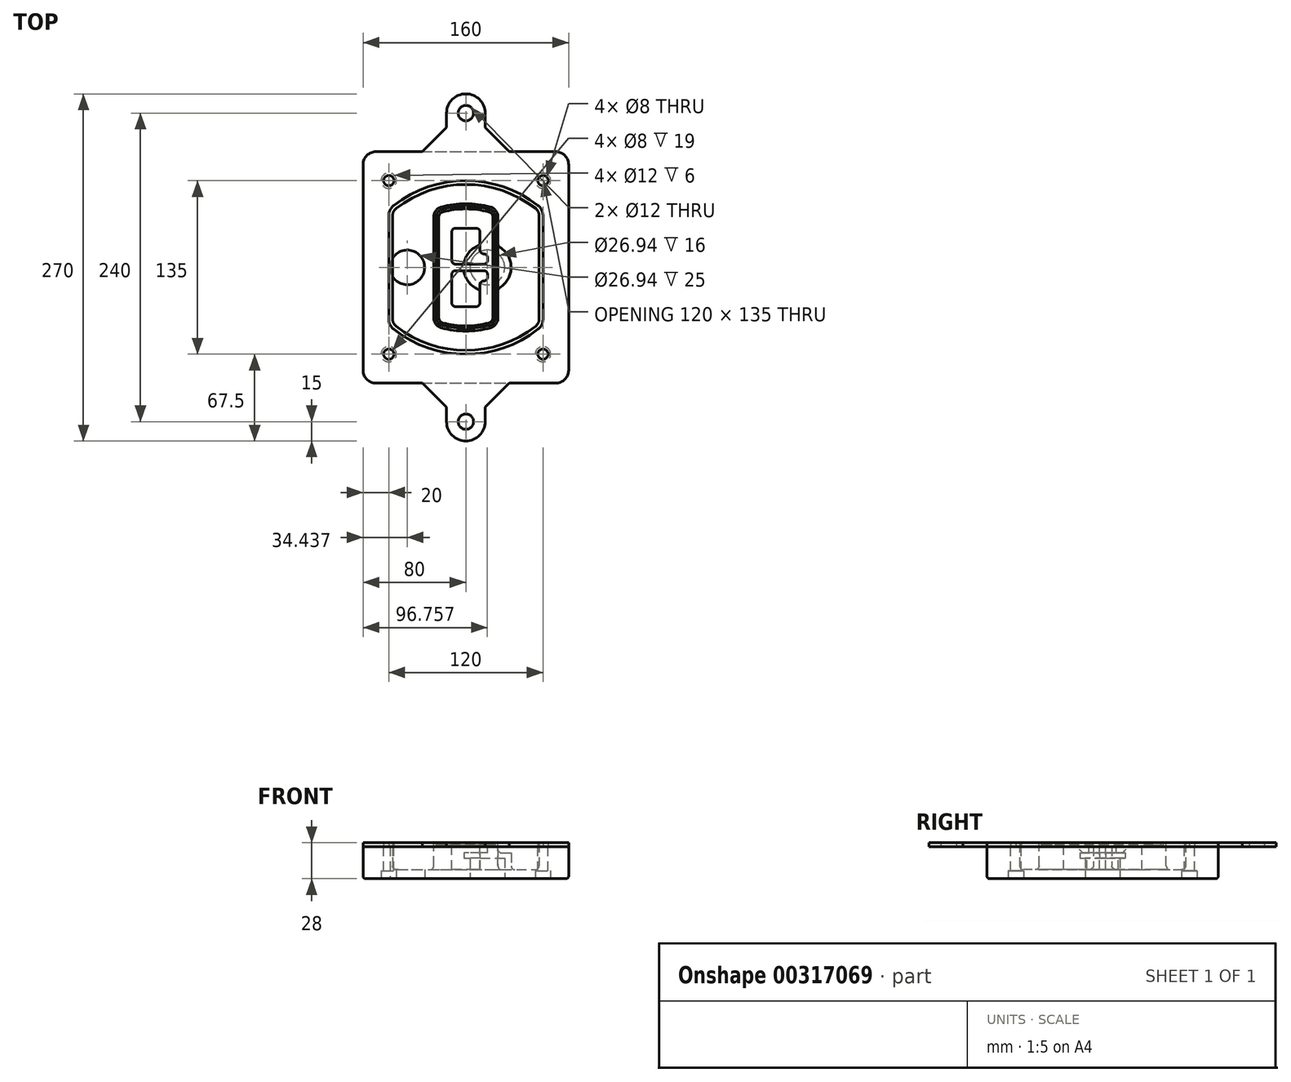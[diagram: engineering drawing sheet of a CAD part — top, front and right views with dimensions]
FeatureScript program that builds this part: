
annotation { "Feature Type Name" : "Feature", "Feature Type Description" : "" }
export const myFeature = defineFeature(function(context is Context, id is Id, definition is map)
    precondition{}
    {
        {
            var Q0;
            Q0=qCreatedBy(makeId("Top.planeOp"),FACE);
            var sketch = newSketch(context, id + "F0", { "sketchPlane" : qUnion([Q0])});
            skPoint(sketch, "E0.rect.middle", {"position": v(0, 0) * mm});
            skLineSegment(sketch, "E1.bottom", {"start": v(-70, -90) * mm, "end": v(70, -90) * mm});
            skLineSegment(sketch, "E1.top", {"start": v(-70, 90) * mm, "end": v(70, 90) * mm});
            skLineSegment(sketch, "E1.left", {"start": v(-80, -80) * mm, "end": v(-80, 80) * mm});
            skLineSegment(sketch, "E1.right", {"start": v(80, -80) * mm, "end": v(80, 80) * mm});
            skLineSegment(sketch, "E2", {"start": v(-80, 90) * mm, "end": v(80, -90) * mm, "construction": true});
            skLineSegment(sketch, "E3", {"start": v(80, 90) * mm, "end": v(-80, -90) * mm, "construction": true});
            skCircle(sketch, "E4", {"center": v(-60, 67.5) * mm, "radius": 4 * mm});
            skCircle(sketch, "E5", {"center": v(60, 67.5) * mm, "radius": 4 * mm});
            skCircle(sketch, "E6", {"center": v(60, -67.5) * mm, "radius": 4 * mm});
            skCircle(sketch, "E7", {"center": v(-60, -67.5) * mm, "radius": 4 * mm});
            skLineSegment(sketch, "E8", {"start": v(-60, 67.5) * mm, "end": v(60, 67.5) * mm, "construction": true});
            skLineSegment(sketch, "E9", {"start": v(60, 67.5) * mm, "end": v(60, -67.5) * mm, "construction": true});
            skLineSegment(sketch, "E10", {"start": v(60, -67.5) * mm, "end": v(-60, -67.5) * mm, "construction": true});
            skLineSegment(sketch, "E11", {"start": v(-60, -67.5) * mm, "end": v(-60, 67.5) * mm, "construction": true});
            skLineSegment(sketch, "E12", {"start": v(-60, 40.3) * mm, "end": v(-60, -40.3) * mm});
            skLineSegment(sketch, "E13", {"start": v(60, 40.3) * mm, "end": v(60, -40.3) * mm});
            skArc(sketch, "E14", {"start": v(56.15, 48.18) * mm, "mid": v(0, 67.5) * mm, "end": v(-56.15, 48.18) * mm});
            skArc(sketch, "E15", {"start": v(-56.15, -48.18) * mm, "mid": v(0, -67.5) * mm, "end": v(56.15, -48.18) * mm});
            skLineSegment(sketch, "E16", {"start": v(-60, 0) * mm, "end": v(60, 0) * mm, "construction": true});
            skPoint(sketch, "E17.visualSharp", {"position": v(-60, -45) * mm});
            skArc(sketch, "E17.filletArc", {"start": v(-60, -40.3) * mm, "mid": v(-58.99, -44.68) * mm, "end": v(-56.15, -48.18) * mm});
            skPoint(sketch, "E18.visualSharp", {"position": v(-60, 45) * mm});
            skArc(sketch, "E18.filletArc", {"start": v(-56.15, 48.18) * mm, "mid": v(-58.99, 44.68) * mm, "end": v(-60, 40.3) * mm});
            skPoint(sketch, "E19.visualSharp", {"position": v(60, 45) * mm});
            skArc(sketch, "E19.filletArc", {"start": v(60, 40.3) * mm, "mid": v(58.99, 44.68) * mm, "end": v(56.15, 48.18) * mm});
            skPoint(sketch, "E20.visualSharp", {"position": v(60, -45) * mm});
            skArc(sketch, "E20.filletArc", {"start": v(56.15, -48.18) * mm, "mid": v(58.99, -44.68) * mm, "end": v(60, -40.3) * mm});
            skPoint(sketch, "E21.visualSharp", {"position": v(-80, 90) * mm});
            skArc(sketch, "E21.filletArc", {"start": v(-70, 90) * mm, "mid": v(-77.07, 87.07) * mm, "end": v(-80, 80) * mm});
            skPoint(sketch, "E22.visualSharp", {"position": v(80, 90) * mm});
            skArc(sketch, "E22.filletArc", {"start": v(80, 80) * mm, "mid": v(77.07, 87.07) * mm, "end": v(70, 90) * mm});
            skPoint(sketch, "E23.visualSharp", {"position": v(80, -90) * mm});
            skArc(sketch, "E23.filletArc", {"start": v(70, -90) * mm, "mid": v(77.07, -87.07) * mm, "end": v(80, -80) * mm});
            skPoint(sketch, "E24.visualSharp", {"position": v(-80, -90) * mm});
            skArc(sketch, "E24.filletArc", {"start": v(-80, -80) * mm, "mid": v(-77.07, -87.07) * mm, "end": v(-70, -90) * mm});
            skArc(sketch, "E25.0", {"start": v(57, 40.3) * mm, "mid": v(56.3, 43.36) * mm, "end": v(54.3, 45.81) * mm});
            skLineSegment(sketch, "E25.1", {"start": v(57, 40.3) * mm, "end": v(57, -40.3) * mm});
            skArc(sketch, "E25.2", {"start": v(54.3, -45.81) * mm, "mid": v(56.3, -43.36) * mm, "end": v(57, -40.3) * mm});
            skArc(sketch, "E25.3", {"start": v(-54.3, -45.81) * mm, "mid": v(0, -64.5) * mm, "end": v(54.3, -45.81) * mm});
            skArc(sketch, "E25.4", {"start": v(-57, -40.3) * mm, "mid": v(-56.3, -43.36) * mm, "end": v(-54.3, -45.81) * mm});
            skArc(sketch, "E25.5", {"start": v(54.3, 45.81) * mm, "mid": v(0, 64.5) * mm, "end": v(-54.3, 45.81) * mm});
            skLineSegment(sketch, "E25.6", {"start": v(-57, 40.3) * mm, "end": v(-57, -40.3) * mm});
            skArc(sketch, "E25.7", {"start": v(-54.3, 45.81) * mm, "mid": v(-56.3, 43.36) * mm, "end": v(-57, 40.3) * mm});
            skArc(sketch, "E26.0", {"start": v(-58.62, 51.33) * mm, "mid": v(-62.58, 46.43) * mm, "end": v(-64, 40.3) * mm});
            skArc(sketch, "E26.1", {"start": v(58.62, 51.33) * mm, "mid": v(0, 71.5) * mm, "end": v(-58.62, 51.33) * mm});
            skArc(sketch, "E26.2", {"start": v(64, 40.3) * mm, "mid": v(62.58, 46.43) * mm, "end": v(58.62, 51.33) * mm});
            skLineSegment(sketch, "E26.3", {"start": v(64, 40.3) * mm, "end": v(64, -40.3) * mm});
            skArc(sketch, "E26.4", {"start": v(58.62, -51.33) * mm, "mid": v(62.58, -46.43) * mm, "end": v(64, -40.3) * mm});
            skLineSegment(sketch, "E26.5", {"start": v(-64, 40.3) * mm, "end": v(-64, -40.3) * mm});
            skArc(sketch, "E26.6", {"start": v(-58.62, -51.33) * mm, "mid": v(0, -71.5) * mm, "end": v(58.62, -51.33) * mm});
            skArc(sketch, "E26.7", {"start": v(-64, -40.3) * mm, "mid": v(-62.58, -46.43) * mm, "end": v(-58.62, -51.33) * mm});
            skSolve(sketch);
        }
        {
            var Q0;
            Q0=makeQuery(id+"F0.imprint","IMPRINT",FACE,{"disambiguationData":[TD([[makeQuery(id+"F0.imprint","IMPRINT",EDGE,{"derivedFrom":sQuery(id+"F0.wireOp",EDGE,"E1.bottom")}),1.0]])]});
            var Q1;
            Q1=makeQuery(id+"F0.imprint","IMPRINT",FACE,{"disambiguationData":[TD([[makeQuery(id+"F0.imprint","IMPRINT",EDGE,{"derivedFrom":sQuery(id+"F0.wireOp",EDGE,"E12")}),1.0]])]});
            var Q2;
            Q2=makeQuery(id+"F0.imprint","IMPRINT",FACE,{"disambiguationData":[TD([[makeQuery(id+"F0.imprint","IMPRINT",EDGE,{"derivedFrom":sQuery(id+"F0.wireOp",EDGE,"E25.0")}),1.0]])]});
            var Q3;
            Q3=makeQuery(id+"F0.imprint","IMPRINT",FACE,{"disambiguationData":[TD([[makeQuery(id+"F0.imprint","IMPRINT",EDGE,{"derivedFrom":sQuery(id+"F0.wireOp",EDGE,"E12")}),-1.0]])]});
            extrude(context, id + "F1", {"entities" : qUnion([Q0, Q1, Q2, Q3]), "oppositeDirection" : true, "depth" : 25 * mm});
        }
        {
            var Q0;
            Q0=makeQuery(id+"F0.imprint","IMPRINT",FACE,{"disambiguationData":[TD([[makeQuery(id+"F0.imprint","IMPRINT",EDGE,{"derivedFrom":sQuery(id+"F0.wireOp",EDGE,"E12")}),1.0]])]});
            extrude(context, id + "F2", {"entities" : qUnion([Q0]), "operationType" : NewBodyOperationType.ADD, "depth" : 3 * mm});
        }
        {
            var Q0;
            Q0=makeQuery(id+"F0.imprint","IMPRINT",FACE,{"disambiguationData":[TD([[makeQuery(id+"F0.imprint","IMPRINT",EDGE,{"derivedFrom":sQuery(id+"F0.wireOp",EDGE,"E25.0")}),1.0]])]});
            extrude(context, id + "F3", {"entities" : qUnion([Q0]), "operationType" : NewBodyOperationType.REMOVE, "oppositeDirection" : true, "depth" : 18 * mm});
        }
        {
            var Q0;
            Q0=makeQuery(id+"F2.opExtrude","CAP_FACE",FACE,{"disambiguationData":[OSD([sQuery(id+"F0.wireOp",EDGE,"E12"),sQuery(id+"F0.wireOp",EDGE,"E13"),sQuery(id+"F0.wireOp",EDGE,"E14"),sQuery(id+"F0.wireOp",EDGE,"E15"),sQuery(id+"F0.wireOp",EDGE,"E17.filletArc"),sQuery(id+"F0.wireOp",EDGE,"E18.filletArc"),sQuery(id+"F0.wireOp",EDGE,"E19.filletArc"),sQuery(id+"F0.wireOp",EDGE,"E20.filletArc"),sQuery(id+"F0.wireOp",EDGE,"E25.0"),sQuery(id+"F0.wireOp",EDGE,"E25.1"),sQuery(id+"F0.wireOp",EDGE,"E25.2"),sQuery(id+"F0.wireOp",EDGE,"E25.3"),sQuery(id+"F0.wireOp",EDGE,"E25.4"),sQuery(id+"F0.wireOp",EDGE,"E25.5"),sQuery(id+"F0.wireOp",EDGE,"E25.6"),sQuery(id+"F0.wireOp",EDGE,"E25.7")])],"isStart":false});
            var sketch = newSketch(context, id + "F4", { "sketchPlane" : qUnion([Q0])});
            skArc(sketch, "E27.0", {"start": v(-19.08, -46.97) * mm, "mid": v(0, -49.5) * mm, "end": v(19.08, -46.97) * mm});
            skArc(sketch, "E28.0", {"start": v(19.08, 46.97) * mm, "mid": v(0, 49.5) * mm, "end": v(-19.08, 46.97) * mm});
            skLineSegment(sketch, "E29", {"start": v(-25, 39.25) * mm, "end": v(-25, -39.25) * mm});
            skLineSegment(sketch, "E30", {"start": v(25, 39.25) * mm, "end": v(25, -39.25) * mm});
            skLineSegment(sketch, "E31", {"start": v(-25, 45.1) * mm, "end": v(25, 45.1) * mm, "construction": true});
            skLineSegment(sketch, "E32", {"start": v(-25, -45.1) * mm, "end": v(25, -45.1) * mm, "construction": true});
            skPoint(sketch, "E33.visualSharp", {"position": v(-25, 45.1) * mm});
            skArc(sketch, "E33.filletArc", {"start": v(-19.08, 46.97) * mm, "mid": v(-23.35, 44.11) * mm, "end": v(-25, 39.25) * mm});
            skPoint(sketch, "E34.visualSharp", {"position": v(25, 45.1) * mm});
            skArc(sketch, "E34.filletArc", {"start": v(25, 39.25) * mm, "mid": v(23.35, 44.11) * mm, "end": v(19.08, 46.97) * mm});
            skPoint(sketch, "E35.visualSharp", {"position": v(25, -45.1) * mm});
            skArc(sketch, "E35.filletArc", {"start": v(19.08, -46.97) * mm, "mid": v(23.35, -44.11) * mm, "end": v(25, -39.25) * mm});
            skPoint(sketch, "E36.visualSharp", {"position": v(-25, -45.1) * mm});
            skArc(sketch, "E36.filletArc", {"start": v(-25, -39.25) * mm, "mid": v(-23.35, -44.11) * mm, "end": v(-19.08, -46.97) * mm});
            skArc(sketch, "E37.0", {"start": v(54.3, 45.81) * mm, "mid": v(0, 64.5) * mm, "end": v(-54.3, 45.81) * mm});
            skArc(sketch, "E37.1", {"start": v(-54.3, 45.81) * mm, "mid": v(-56.3, 43.36) * mm, "end": v(-57, 40.3) * mm});
            skLineSegment(sketch, "E37.2", {"start": v(-57, 40.3) * mm, "end": v(-57, -40.3) * mm});
            skArc(sketch, "E37.3", {"start": v(-57, -40.3) * mm, "mid": v(-56.3, -43.36) * mm, "end": v(-54.3, -45.81) * mm});
            skArc(sketch, "E37.4", {"start": v(-54.3, -45.81) * mm, "mid": v(0, -64.5) * mm, "end": v(54.3, -45.81) * mm});
            skArc(sketch, "E37.5", {"start": v(54.3, -45.81) * mm, "mid": v(56.3, -43.36) * mm, "end": v(57, -40.3) * mm});
            skLineSegment(sketch, "E37.6", {"start": v(57, 40.3) * mm, "end": v(57, -40.3) * mm});
            skArc(sketch, "E37.7", {"start": v(57, 40.3) * mm, "mid": v(56.3, 43.36) * mm, "end": v(54.3, 45.81) * mm});
            skLineSegment(sketch, "E38.0", {"start": v(23, 39.25) * mm, "end": v(23, -39.25) * mm});
            skArc(sketch, "E38.1", {"start": v(18.56, -45.04) * mm, "mid": v(21.76, -42.9) * mm, "end": v(23, -39.25) * mm});
            skArc(sketch, "E38.2", {"start": v(-18.56, -45.04) * mm, "mid": v(0, -47.5) * mm, "end": v(18.56, -45.04) * mm});
            skArc(sketch, "E38.3", {"start": v(-23, -39.25) * mm, "mid": v(-21.76, -42.9) * mm, "end": v(-18.56, -45.04) * mm});
            skLineSegment(sketch, "E38.4", {"start": v(-23, 39.25) * mm, "end": v(-23, -39.25) * mm});
            skArc(sketch, "E38.5", {"start": v(23, 39.25) * mm, "mid": v(21.76, 42.9) * mm, "end": v(18.56, 45.04) * mm});
            skArc(sketch, "E38.6", {"start": v(-18.56, 45.04) * mm, "mid": v(-21.76, 42.9) * mm, "end": v(-23, 39.25) * mm});
            skArc(sketch, "E38.7", {"start": v(18.56, 45.04) * mm, "mid": v(0, 47.5) * mm, "end": v(-18.56, 45.04) * mm});
            skArc(sketch, "E39.0", {"start": v(21, 39.25) * mm, "mid": v(20.18, 41.68) * mm, "end": v(18.04, 43.1) * mm});
            skLineSegment(sketch, "E39.1", {"start": v(21, 39.25) * mm, "end": v(21, -39.25) * mm});
            skArc(sketch, "E39.2", {"start": v(18.04, -43.1) * mm, "mid": v(20.18, -41.68) * mm, "end": v(21, -39.25) * mm});
            skArc(sketch, "E39.3", {"start": v(-18.04, -43.1) * mm, "mid": v(0, -45.5) * mm, "end": v(18.04, -43.1) * mm});
            skArc(sketch, "E39.4", {"start": v(-21, -39.25) * mm, "mid": v(-20.18, -41.68) * mm, "end": v(-18.04, -43.1) * mm});
            skArc(sketch, "E39.5", {"start": v(18.04, 43.1) * mm, "mid": v(0, 45.5) * mm, "end": v(-18.04, 43.1) * mm});
            skLineSegment(sketch, "E39.6", {"start": v(-21, 39.25) * mm, "end": v(-21, -39.25) * mm});
            skArc(sketch, "E39.7", {"start": v(-18.04, 43.1) * mm, "mid": v(-20.18, 41.68) * mm, "end": v(-21, 39.25) * mm});
            skLineSegment(sketch, "E40", {"start": v(-25, 0) * mm, "end": v(25, 0) * mm, "construction": true});
            skLineSegment(sketch, "E41", {"start": v(-11, 5.5) * mm, "end": v(-11, 27.5) * mm});
            skLineSegment(sketch, "E42", {"start": v(-8, 30.5) * mm, "end": v(8, 30.5) * mm});
            skLineSegment(sketch, "E43", {"start": v(11, 27.5) * mm, "end": v(11, 13.5) * mm});
            skLineSegment(sketch, "E44", {"start": v(14, 10.5) * mm, "end": v(14, 10.5) * mm});
            skLineSegment(sketch, "E45", {"start": v(17, 7.5) * mm, "end": v(17, 5.5) * mm});
            skLineSegment(sketch, "E46", {"start": v(14, 2.5) * mm, "end": v(-8, 2.5) * mm});
            skPoint(sketch, "E47.visualSharp", {"position": v(-11, 30.5) * mm});
            skArc(sketch, "E47.filletArc", {"start": v(-8, 30.5) * mm, "mid": v(-10.12, 29.62) * mm, "end": v(-11, 27.5) * mm});
            skPoint(sketch, "E48.visualSharp", {"position": v(11, 30.5) * mm});
            skArc(sketch, "E48.filletArc", {"start": v(11, 27.5) * mm, "mid": v(10.12, 29.62) * mm, "end": v(8, 30.5) * mm});
            skPoint(sketch, "E49.visualSharp", {"position": v(11, 10.5) * mm});
            skArc(sketch, "E49.filletArc", {"start": v(11, 13.5) * mm, "mid": v(11.88, 11.38) * mm, "end": v(14, 10.5) * mm});
            skPoint(sketch, "E50.visualSharp", {"position": v(17, 10.5) * mm});
            skArc(sketch, "E50.filletArc", {"start": v(17, 7.5) * mm, "mid": v(16.12, 9.62) * mm, "end": v(14, 10.5) * mm});
            skPoint(sketch, "E51.visualSharp", {"position": v(17, 2.5) * mm});
            skArc(sketch, "E51.filletArc", {"start": v(14, 2.5) * mm, "mid": v(16.12, 3.38) * mm, "end": v(17, 5.5) * mm});
            skPoint(sketch, "E52.visualSharp", {"position": v(-11, 2.5) * mm});
            skArc(sketch, "E52.filletArc", {"start": v(-11, 5.5) * mm, "mid": v(-10.12, 3.38) * mm, "end": v(-8, 2.5) * mm});
            skLineSegment(sketch, "E53.0.MirrorCS", {"start": v(14, -2.5) * mm, "end": v(-8, -2.5) * mm});
            skArc(sketch, "E54.0.MirrorCS", {"start": v(-11, -5.5) * mm, "mid": v(-10.12, -3.38) * mm, "end": v(-8, -2.5) * mm});
            skLineSegment(sketch, "E55.0.MirrorCS", {"start": v(-11, -5.5) * mm, "end": v(-11, -27.5) * mm});
            skArc(sketch, "E56.0.MirrorCS", {"start": v(-8, -30.5) * mm, "mid": v(-10.12, -29.62) * mm, "end": v(-11, -27.5) * mm});
            skLineSegment(sketch, "E57.0.MirrorCS", {"start": v(-8, -30.5) * mm, "end": v(8, -30.5) * mm});
            skArc(sketch, "E58.0.MirrorCS", {"start": v(11, -27.5) * mm, "mid": v(10.12, -29.62) * mm, "end": v(8, -30.5) * mm});
            skLineSegment(sketch, "E59.0.MirrorCS", {"start": v(11, -27.5) * mm, "end": v(11, -13.5) * mm});
            skArc(sketch, "E60.0.MirrorCS", {"start": v(11, -13.5) * mm, "mid": v(11.88, -11.38) * mm, "end": v(14, -10.5) * mm});
            skArc(sketch, "E61.0.MirrorCS", {"start": v(17, -7.5) * mm, "mid": v(16.12, -9.62) * mm, "end": v(14, -10.5) * mm});
            skLineSegment(sketch, "E62.0.MirrorCS", {"start": v(17, -7.5) * mm, "end": v(17, -5.5) * mm});
            skArc(sketch, "E63.0.MirrorCS", {"start": v(14, -2.5) * mm, "mid": v(16.12, -3.38) * mm, "end": v(17, -5.5) * mm});
            skSolve(sketch);
        }
        {
            var Q0;
            Q0=makeQuery(id+"F4.imprint","IMPRINT",FACE,{"disambiguationData":[TD([[makeQuery(id+"F4.imprint","IMPRINT",EDGE,{"derivedFrom":sQuery(id+"F4.wireOp",EDGE,"E27.0")}),1.0]])]});
            var Q1;
            Q1=makeQuery(id+"F4.imprint","IMPRINT",FACE,{"disambiguationData":[TD([[makeQuery(id+"F4.imprint","IMPRINT",EDGE,{"derivedFrom":sQuery(id+"F4.wireOp",EDGE,"E38.0")}),-1.0]])]});
            var Q2;
            Q2=makeQuery(id+"F4.imprint","IMPRINT",FACE,{"disambiguationData":[TD([[makeQuery(id+"F4.imprint","IMPRINT",EDGE,{"derivedFrom":sQuery(id+"F4.wireOp",EDGE,"E39.0")}),1.0]])]});
            extrude(context, id + "F5", {"entities" : qUnion([Q0, Q1, Q2]), "operationType" : NewBodyOperationType.ADD, "endBound" : BoundingType.UP_TO_NEXT, "oppositeDirection" : true, "depth" : 25 * mm});
        }
        {
            var Q0;
            Q0=makeQuery(id+"F4.imprint","IMPRINT",FACE,{"disambiguationData":[TD([[makeQuery(id+"F4.imprint","IMPRINT",EDGE,{"derivedFrom":sQuery(id+"F4.wireOp",EDGE,"E38.0")}),-1.0]])]});
            extrude(context, id + "F6", {"entities" : qUnion([Q0]), "operationType" : NewBodyOperationType.REMOVE, "oppositeDirection" : true, "depth" : 2 * mm});
        }
        {
            var Q0;
            Q0=makeQuery(id+"F1.opExtrude","CAP_FACE",FACE,{"disambiguationData":[OSD([sQuery(id+"F0.wireOp",EDGE,"E1.bottom"),sQuery(id+"F0.wireOp",EDGE,"E1.top"),sQuery(id+"F0.wireOp",EDGE,"E1.left"),sQuery(id+"F0.wireOp",EDGE,"E1.right"),sQuery(id+"F0.wireOp",EDGE,"E4"),sQuery(id+"F0.wireOp",EDGE,"E5"),sQuery(id+"F0.wireOp",EDGE,"E6"),sQuery(id+"F0.wireOp",EDGE,"E7"),sQuery(id+"F0.wireOp",EDGE,"E21.filletArc"),sQuery(id+"F0.wireOp",EDGE,"E22.filletArc"),sQuery(id+"F0.wireOp",EDGE,"E23.filletArc"),sQuery(id+"F0.wireOp",EDGE,"E24.filletArc")])],"isStart":false});
            var sketch = newSketch(context, id + "F7", { "sketchPlane" : qUnion([Q0])});
            skCircle(sketch, "E64", {"center": v(16.76, 0) * mm, "radius": 13.47 * mm});
            skCircle(sketch, "E65", {"center": v(-45.56, 0) * mm, "radius": 13.47 * mm});
            skLineSegment(sketch, "E66", {"start": v(80, 0) * mm, "end": v(-80, 0) * mm});
            skCircle(sketch, "E67", {"center": v(16.76, 0) * mm, "radius": 18.47 * mm});
            skCircle(sketch, "E68", {"center": v(60, -67.5) * mm, "radius": 6 * mm});
            skCircle(sketch, "E69", {"center": v(-60, -67.5) * mm, "radius": 6 * mm});
            skCircle(sketch, "E70", {"center": v(-60, 67.5) * mm, "radius": 6 * mm});
            skCircle(sketch, "E71", {"center": v(60, 67.5) * mm, "radius": 6 * mm});
            skSolve(sketch);
        }
        {
            var Q0;
            {var subQ1=sQuery(id+"F7.wireOp",EDGE,"E66");var subQ4=sQuery(id+"F7.wireOp",EDGE,"E64");var subQ6=makeQuery(id+"F7.imprint","INTERSECT",VERTEX,{"disambiguationData":[OD(0.0)],"derivedFrom":[subQ4,subQ1]});Q0=makeQuery(id+"F7.imprint","IMPRINT",FACE,{"disambiguationData":[TD([[makeQuery(id+"F7.imprint","IMPRINT",EDGE,{"disambiguationData":[TD([[subQ6,-1.0]])],"derivedFrom":subQ4}),-1.0]])]});}
            var Q1;
            {var subQ0=sQuery(id+"F7.wireOp",EDGE,"E66");var subQ1=sQuery(id+"F7.wireOp",EDGE,"E64");var subQ3=makeQuery(id+"F7.imprint","INTERSECT",VERTEX,{"disambiguationData":[OD(0.0)],"derivedFrom":[subQ1,subQ0]});Q1=makeQuery(id+"F7.imprint","IMPRINT",FACE,{"disambiguationData":[TD([[makeQuery(id+"F7.imprint","IMPRINT",EDGE,{"disambiguationData":[TD([[subQ3,-1.0]])],"derivedFrom":subQ1}),1.0]])]});}
            var Q2;
            {var subQ0=sQuery(id+"F7.wireOp",EDGE,"E66");var subQ1=sQuery(id+"F7.wireOp",EDGE,"E64");var subQ3=makeQuery(id+"F7.imprint","INTERSECT",VERTEX,{"disambiguationData":[OD(0.0)],"derivedFrom":[subQ1,subQ0]});Q2=makeQuery(id+"F7.imprint","IMPRINT",FACE,{"disambiguationData":[TD([[makeQuery(id+"F7.imprint","IMPRINT",EDGE,{"disambiguationData":[TD([[subQ3,1.0]])],"derivedFrom":subQ1}),1.0]])]});}
            var Q3;
            {var subQ1=sQuery(id+"F7.wireOp",EDGE,"E66");var subQ4=sQuery(id+"F7.wireOp",EDGE,"E64");var subQ6=makeQuery(id+"F7.imprint","INTERSECT",VERTEX,{"disambiguationData":[OD(0.0)],"derivedFrom":[subQ4,subQ1]});Q3=makeQuery(id+"F7.imprint","IMPRINT",FACE,{"disambiguationData":[TD([[makeQuery(id+"F7.imprint","IMPRINT",EDGE,{"disambiguationData":[TD([[subQ6,1.0]])],"derivedFrom":subQ4}),-1.0]])]});}
            extrude(context, id + "F8", {"entities" : qUnion([Q0, Q1, Q2, Q3]), "operationType" : NewBodyOperationType.ADD, "oppositeDirection" : true, "depth" : 20 * mm});
        }
        {
            var Q0;
            {var subQ0=sQuery(id+"F7.wireOp",EDGE,"E66");var subQ1=sQuery(id+"F7.wireOp",EDGE,"E64");var subQ3=makeQuery(id+"F7.imprint","INTERSECT",VERTEX,{"disambiguationData":[OD(0.0)],"derivedFrom":[subQ1,subQ0]});Q0=makeQuery(id+"F7.imprint","IMPRINT",FACE,{"disambiguationData":[TD([[makeQuery(id+"F7.imprint","IMPRINT",EDGE,{"disambiguationData":[TD([[subQ3,-1.0]])],"derivedFrom":subQ1}),1.0]])]});}
            var Q1;
            {var subQ0=sQuery(id+"F7.wireOp",EDGE,"E66");var subQ1=sQuery(id+"F7.wireOp",EDGE,"E64");var subQ3=makeQuery(id+"F7.imprint","INTERSECT",VERTEX,{"disambiguationData":[OD(0.0)],"derivedFrom":[subQ1,subQ0]});Q1=makeQuery(id+"F7.imprint","IMPRINT",FACE,{"disambiguationData":[TD([[makeQuery(id+"F7.imprint","IMPRINT",EDGE,{"disambiguationData":[TD([[subQ3,1.0]])],"derivedFrom":subQ1}),1.0]])]});}
            extrude(context, id + "F9", {"entities" : qUnion([Q0, Q1]), "operationType" : NewBodyOperationType.REMOVE, "oppositeDirection" : true, "depth" : 16 * mm});
        }
        {
            var Q0;
            {var subQ0=sQuery(id+"F7.wireOp",EDGE,"E66");var subQ1=sQuery(id+"F7.wireOp",EDGE,"E65");var subQ3=makeQuery(id+"F7.imprint","INTERSECT",VERTEX,{"disambiguationData":[OD(0.0)],"derivedFrom":[subQ1,subQ0]});Q0=makeQuery(id+"F7.imprint","IMPRINT",FACE,{"disambiguationData":[TD([[makeQuery(id+"F7.imprint","IMPRINT",EDGE,{"disambiguationData":[TD([[subQ3,-1.0]])],"derivedFrom":subQ1}),1.0]])]});}
            var Q1;
            {var subQ0=sQuery(id+"F7.wireOp",EDGE,"E66");var subQ1=sQuery(id+"F7.wireOp",EDGE,"E65");var subQ3=makeQuery(id+"F7.imprint","INTERSECT",VERTEX,{"disambiguationData":[OD(0.0)],"derivedFrom":[subQ1,subQ0]});Q1=makeQuery(id+"F7.imprint","IMPRINT",FACE,{"disambiguationData":[TD([[makeQuery(id+"F7.imprint","IMPRINT",EDGE,{"disambiguationData":[TD([[subQ3,1.0]])],"derivedFrom":subQ1}),1.0]])]});}
            extrude(context, id + "F10", {"entities" : qUnion([Q0, Q1]), "operationType" : NewBodyOperationType.REMOVE, "oppositeDirection" : true, "depth" : 25 * mm});
        }
        {
            var Q0;
            Q0=makeQuery(id+"F7.imprint","IMPRINT",FACE,{"disambiguationData":[TD([[makeQuery(id+"F7.imprint","IMPRINT",EDGE,{"derivedFrom":sQuery(id+"F7.wireOp",EDGE,"E68")}),1.0]])]});
            var Q1;
            Q1=makeQuery(id+"F7.imprint","IMPRINT",FACE,{"disambiguationData":[TD([[makeQuery(id+"F7.imprint","IMPRINT",EDGE,{"derivedFrom":makeQuery(id+"F1.opExtrude","CAP_EDGE",EDGE,{"disambiguationData":[OSD([sQuery(id+"F0.wireOp",EDGE,"E5")])],"isStart":false})}),-1.0]])]});
            var Q2;
            Q2=makeQuery(id+"F7.imprint","IMPRINT",FACE,{"disambiguationData":[TD([[makeQuery(id+"F7.imprint","IMPRINT",EDGE,{"derivedFrom":sQuery(id+"F7.wireOp",EDGE,"E69")}),1.0]])]});
            var Q3;
            Q3=makeQuery(id+"F7.imprint","IMPRINT",FACE,{"disambiguationData":[TD([[makeQuery(id+"F7.imprint","IMPRINT",EDGE,{"derivedFrom":makeQuery(id+"F1.opExtrude","CAP_EDGE",EDGE,{"disambiguationData":[OSD([sQuery(id+"F0.wireOp",EDGE,"E4")])],"isStart":false})}),-1.0]])]});
            var Q4;
            Q4=makeQuery(id+"F7.imprint","IMPRINT",FACE,{"disambiguationData":[TD([[makeQuery(id+"F7.imprint","IMPRINT",EDGE,{"derivedFrom":sQuery(id+"F7.wireOp",EDGE,"E70")}),1.0]])]});
            var Q5;
            Q5=makeQuery(id+"F7.imprint","IMPRINT",FACE,{"disambiguationData":[TD([[makeQuery(id+"F7.imprint","IMPRINT",EDGE,{"derivedFrom":makeQuery(id+"F1.opExtrude","CAP_EDGE",EDGE,{"disambiguationData":[OSD([sQuery(id+"F0.wireOp",EDGE,"E7")])],"isStart":false})}),-1.0]])]});
            var Q6;
            Q6=makeQuery(id+"F7.imprint","IMPRINT",FACE,{"disambiguationData":[TD([[makeQuery(id+"F7.imprint","IMPRINT",EDGE,{"derivedFrom":sQuery(id+"F7.wireOp",EDGE,"E71")}),1.0]])]});
            var Q7;
            Q7=makeQuery(id+"F7.imprint","IMPRINT",FACE,{"disambiguationData":[TD([[makeQuery(id+"F7.imprint","IMPRINT",EDGE,{"derivedFrom":makeQuery(id+"F1.opExtrude","CAP_EDGE",EDGE,{"disambiguationData":[OSD([sQuery(id+"F0.wireOp",EDGE,"E6")])],"isStart":false})}),-1.0]])]});
            extrude(context, id + "F11", {"entities" : qUnion([Q0, Q1, Q2, Q3, Q4, Q5, Q6, Q7]), "operationType" : NewBodyOperationType.REMOVE, "oppositeDirection" : true, "depth" : 6 * mm});
        }
        {
            var Q0;
            Q0=makeQuery(id+"F9.boolean.opBoolean","COPY",FACE,{"derivedFrom":makeQuery(id+"F9.opExtrude","CAP_FACE",FACE,{"disambiguationData":[OSD([sQuery(id+"F7.wireOp",EDGE,"E64")])],"isStart":false})});
            var sketch = newSketch(context, id + "F12", { "sketchPlane" : qUnion([Q0])});
            skArc(sketch, "E72.0", {"start": v(11, 17.55) * mm, "mid": v(2.57, 11.82) * mm, "end": v(-1.54, 2.5) * mm});
            skArc(sketch, "E72.1", {"start": v(-1.54, -2.5) * mm, "mid": v(2.57, -11.82) * mm, "end": v(11, -17.55) * mm});
            skLineSegment(sketch, "E73", {"start": v(-1.54, -2.5) * mm, "end": v(14, -2.5) * mm});
            skLineSegment(sketch, "E74.0", {"start": v(14, 2.5) * mm, "end": v(-1.54, 2.5) * mm});
            skArc(sketch, "E74.1", {"start": v(14, 2.5) * mm, "mid": v(16.12, 3.38) * mm, "end": v(17, 5.5) * mm});
            skLineSegment(sketch, "E74.2", {"start": v(17, 7.5) * mm, "end": v(17, 5.5) * mm});
            skArc(sketch, "E74.3", {"start": v(17, 7.5) * mm, "mid": v(16.12, 9.62) * mm, "end": v(14, 10.5) * mm});
            skArc(sketch, "E74.4", {"start": v(11, 13.5) * mm, "mid": v(11.88, 11.38) * mm, "end": v(14, 10.5) * mm});
            skLineSegment(sketch, "E74.5", {"start": v(11, 17.55) * mm, "end": v(11, 13.5) * mm});
            skLineSegment(sketch, "E74.7", {"start": v(14, -2.5) * mm, "end": v(-1.54, -2.5) * mm});
            skArc(sketch, "E74.8", {"start": v(14, -2.5) * mm, "mid": v(16.12, -3.38) * mm, "end": v(17, -5.5) * mm});
            skLineSegment(sketch, "E74.9", {"start": v(17, -7.5) * mm, "end": v(17, -5.5) * mm});
            skArc(sketch, "E74.10", {"start": v(17, -7.5) * mm, "mid": v(16.12, -9.62) * mm, "end": v(14, -10.5) * mm});
            skArc(sketch, "E74.11", {"start": v(11, -13.5) * mm, "mid": v(11.88, -11.38) * mm, "end": v(14, -10.5) * mm});
            skLineSegment(sketch, "E74.12", {"start": v(11, -17.55) * mm, "end": v(11, -13.5) * mm});
            skPoint(sketch, "E75.orphan", {"position": v(11, -27.5) * mm});
            skPoint(sketch, "E76.orphan", {"position": v(-8, -2.5) * mm});
            skPoint(sketch, "E77.orphan", {"position": v(-8, 2.5) * mm});
            skPoint(sketch, "E78.orphan", {"position": v(11, 27.5) * mm});
            skSolve(sketch);
        }
        {
            var Q0;
            {var subQ7=sQuery(id+"F12.wireOp",EDGE,"E72.0");var subQ14=sQuery(id+"F12.wireOp",EDGE,"E72.1");var subQ16=sQuery(id+"F12.wireOp",EDGE,"E74.1");var subQ18=sQuery(id+"F12.wireOp",EDGE,"E74.8");Q0=qUnion([makeQuery(id+"F12.imprint","IMPRINT",FACE,{"disambiguationData":[TD([[makeQuery(id+"F12.imprint","IMPRINT",EDGE,{"derivedFrom":subQ7}),1.0]])]}),makeQuery(id+"F12.imprint","IMPRINT",FACE,{"disambiguationData":[TD([[makeQuery(id+"F12.imprint","IMPRINT",EDGE,{"derivedFrom":subQ14}),1.0]])]}),makeQuery(id+"F12.imprint","IMPRINT",FACE,{"disambiguationData":[TD([[makeQuery(id+"F12.imprint","IMPRINT",EDGE,{"derivedFrom":subQ16}),1.0]])]}),makeQuery(id+"F12.imprint","IMPRINT",FACE,{"disambiguationData":[TD([[makeQuery(id+"F12.imprint","IMPRINT",EDGE,{"derivedFrom":subQ18}),-1.0]])]})]);}
            var Q1;
            Q1=makeQuery(id+"F5.boolean.opBoolean","SPLIT",FACE,{"disambiguationData":[TD([makeQuery(id+"F5.opExtrude","SWEPT_FACE",FACE,{"disambiguationData":[OSD([sQuery(id+"F4.wireOp",EDGE,"E41")])]})])],"derivedFrom":makeQuery(id+"F3.boolean.opBoolean","COPY",FACE,{"derivedFrom":makeQuery(id+"F3.opExtrude","CAP_FACE",FACE,{"disambiguationData":[OSD([sQuery(id+"F0.wireOp",EDGE,"E25.0"),sQuery(id+"F0.wireOp",EDGE,"E25.1"),sQuery(id+"F0.wireOp",EDGE,"E25.2"),sQuery(id+"F0.wireOp",EDGE,"E25.3"),sQuery(id+"F0.wireOp",EDGE,"E25.4"),sQuery(id+"F0.wireOp",EDGE,"E25.5"),sQuery(id+"F0.wireOp",EDGE,"E25.6"),sQuery(id+"F0.wireOp",EDGE,"E25.7")])],"isStart":false})})});
            extrude(context, id + "F13", {"entities" : qUnion([Q0]), "operationType" : NewBodyOperationType.REMOVE, "endBound" : BoundingType.UP_TO_SURFACE, "endBoundEntityFace" : qUnion([Q1]), "depth" : 25 * mm});
        }
        {
            var Q0;
            Q0=makeQuery(id+"F3.boolean.opBoolean","COPY",EDGE,{"derivedFrom":makeQuery(id+"F3.opExtrude","CAP_EDGE",EDGE,{"disambiguationData":[OSD([sQuery(id+"F0.wireOp",EDGE,"E25.6")])],"isStart":false})});
            var Q1;
            Q1=makeQuery(id+"F8.boolean.opBoolean","INTERSECT",EDGE,{"derivedFrom":[makeQuery(id+"F5.opExtrude","SWEPT_FACE",FACE,{"disambiguationData":[OSD([sQuery(id+"F4.wireOp",EDGE,"E30")])]}),makeQuery(id+"F8.opExtrude","CAP_FACE",FACE,{"disambiguationData":[OSD([sQuery(id+"F7.wireOp",EDGE,"E67")])],"isStart":false})]});
            var Q2;
            Q2=makeQuery(id+"F8.boolean.opBoolean","INTERSECT",EDGE,{"disambiguationData":[OD(1.0)],"derivedFrom":[makeQuery(id+"F5.opExtrude","SWEPT_FACE",FACE,{"disambiguationData":[OSD([sQuery(id+"F4.wireOp",EDGE,"E30")])]}),makeQuery(id+"F8.opExtrude","SWEPT_FACE",FACE,{"disambiguationData":[OSD([sQuery(id+"F7.wireOp",EDGE,"E67")])]})]});
            var Q3;
            {var subQ0=sQuery(id+"F4.wireOp",EDGE,"E30");Q3=makeQuery(id+"F8.boolean.opBoolean","SPLIT",EDGE,{"disambiguationData":[TD([makeQuery(id+"F5.opExtrude","SWEPT_FACE",FACE,{"disambiguationData":[OSD([sQuery(id+"F4.wireOp",EDGE,"E35.filletArc")])]})])],"derivedFrom":makeQuery(id+"F5.opExtrude","CAP_EDGE",EDGE,{"disambiguationData":[OSD([subQ0])],"isStart":false})});}
            var Q4;
            {var subQ0=sQuery(id+"F0.wireOp",EDGE,"E25.7");var subQ1=sQuery(id+"F0.wireOp",EDGE,"E25.1");var subQ2=sQuery(id+"F0.wireOp",EDGE,"E25.6");var subQ3=sQuery(id+"F0.wireOp",EDGE,"E25.5");var subQ4=sQuery(id+"F0.wireOp",EDGE,"E25.4");var subQ5=sQuery(id+"F0.wireOp",EDGE,"E25.0");var subQ6=sQuery(id+"F0.wireOp",EDGE,"E25.2");var subQ7=sQuery(id+"F0.wireOp",EDGE,"E25.3");Q4=makeQuery(id+"F8.boolean.opBoolean","INTERSECT",EDGE,{"derivedFrom":[makeQuery(id+"F5.boolean.opBoolean","SPLIT",FACE,{"disambiguationData":[TD([makeQuery(id+"F2.opExtrude","SWEPT_FACE",FACE,{"disambiguationData":[OSD([subQ5])]})])],"derivedFrom":makeQuery(id+"F3.boolean.opBoolean","COPY",FACE,{"derivedFrom":makeQuery(id+"F3.opExtrude","CAP_FACE",FACE,{"disambiguationData":[OSD([subQ5,subQ1,subQ6,subQ7,subQ4,subQ3,subQ2,subQ0])],"isStart":false})})}),makeQuery(id+"F8.opExtrude","SWEPT_FACE",FACE,{"disambiguationData":[OSD([sQuery(id+"F7.wireOp",EDGE,"E67")])]})]});}
            var Q5;
            Q5=makeQuery(id+"F8.boolean.opBoolean","INTERSECT",EDGE,{"disambiguationData":[OD(0.0)],"derivedFrom":[makeQuery(id+"F5.opExtrude","SWEPT_FACE",FACE,{"disambiguationData":[OSD([sQuery(id+"F4.wireOp",EDGE,"E30")])]}),makeQuery(id+"F8.opExtrude","SWEPT_FACE",FACE,{"disambiguationData":[OSD([sQuery(id+"F7.wireOp",EDGE,"E67")])]})]});
            fillet(context, id + "F14", {"entities" : qUnion([Q0, Q1, Q2, Q3, Q4, Q5]), "radius" : 3 * mm, "tangentPropagation" : true, "allowEdgeOverflow" : false});
        }
        {
            var Q0;
            Q0=makeQuery(id+"F1.opExtrude","CAP_EDGE",EDGE,{"disambiguationData":[OSD([sQuery(id+"F0.wireOp",EDGE,"E1.bottom")])],"isStart":false});
            fillet(context, id + "F15", {"entities" : qUnion([Q0]), "radius" : 2 * mm, "tangentPropagation" : true, "allowEdgeOverflow" : false});
        }
        {
            var Q0;
            {var subQ0=sQuery(id+"F0.wireOp",EDGE,"E21.filletArc");var subQ1=sQuery(id+"F0.wireOp",EDGE,"E7");var subQ2=sQuery(id+"F0.wireOp",EDGE,"E6");var subQ3=sQuery(id+"F0.wireOp",EDGE,"E5");var subQ4=sQuery(id+"F0.wireOp",EDGE,"E4");var subQ5=sQuery(id+"F0.wireOp",EDGE,"E22.filletArc");var subQ6=sQuery(id+"F0.wireOp",EDGE,"E1.bottom");var subQ7=sQuery(id+"F0.wireOp",EDGE,"E1.right");var subQ8=sQuery(id+"F0.wireOp",EDGE,"E1.top");var subQ9=sQuery(id+"F0.wireOp",EDGE,"E1.left");var subQ10=sQuery(id+"F0.wireOp",EDGE,"E23.filletArc");var subQ11=sQuery(id+"F0.wireOp",EDGE,"E24.filletArc");Q0=makeQuery(id+"F2.boolean.opBoolean","SPLIT",FACE,{"disambiguationData":[TD([makeQuery(id+"F1.opExtrude","SWEPT_FACE",FACE,{"disambiguationData":[OSD([subQ6])]})])],"derivedFrom":makeQuery(id+"F1.opExtrude","CAP_FACE",FACE,{"disambiguationData":[OSD([subQ6,subQ8,subQ9,subQ7,subQ4,subQ3,subQ2,subQ1,subQ0,subQ5,subQ10,subQ11])],"isStart":true})});}
            var sketch = newSketch(context, id + "F16", { "sketchPlane" : qUnion([Q0])});
            skLineSegment(sketch, "E79.0", {"start": v(-80, -80) * mm, "end": v(-80, 80) * mm});
            skArc(sketch, "E79.1", {"start": v(-70, 90) * mm, "mid": v(-77.07, 87.07) * mm, "end": v(-80, 80) * mm});
            skLineSegment(sketch, "E79.2", {"start": v(-70, 90) * mm, "end": v(70, 90) * mm});
            skLineSegment(sketch, "E79.3", {"start": v(80, -80) * mm, "end": v(80, 80) * mm});
            skArc(sketch, "E79.4", {"start": v(80, 80) * mm, "mid": v(77.07, 87.07) * mm, "end": v(70, 90) * mm});
            skArc(sketch, "E79.5", {"start": v(70, -90) * mm, "mid": v(77.07, -87.07) * mm, "end": v(80, -80) * mm});
            skLineSegment(sketch, "E79.6", {"start": v(-70, -90) * mm, "end": v(70, -90) * mm});
            skArc(sketch, "E79.7", {"start": v(-80, -80) * mm, "mid": v(-77.07, -87.07) * mm, "end": v(-70, -90) * mm});
            skCircle(sketch, "E79.8", {"center": v(-60, -67.5) * mm, "radius": 4 * mm});
            skCircle(sketch, "E79.9", {"center": v(-60, 67.5) * mm, "radius": 4 * mm});
            skCircle(sketch, "E79.10", {"center": v(60, 67.5) * mm, "radius": 4 * mm});
            skCircle(sketch, "E79.11", {"center": v(60, -67.5) * mm, "radius": 4 * mm});
            skArc(sketch, "E79.12", {"start": v(-56.15, -48.18) * mm, "mid": v(0, -67.5) * mm, "end": v(56.15, -48.18) * mm});
            skLineSegment(sketch, "E79.13", {"start": v(60, 40.3) * mm, "end": v(60, -40.3) * mm});
            skArc(sketch, "E79.14", {"start": v(56.15, 48.18) * mm, "mid": v(0, 67.5) * mm, "end": v(-56.15, 48.18) * mm});
            skArc(sketch, "E79.15", {"start": v(60, 40.3) * mm, "mid": v(58.99, 44.68) * mm, "end": v(56.15, 48.18) * mm});
            skArc(sketch, "E79.16", {"start": v(-56.15, 48.18) * mm, "mid": v(-58.99, 44.68) * mm, "end": v(-60, 40.3) * mm});
            skLineSegment(sketch, "E79.17", {"start": v(-60, 40.3) * mm, "end": v(-60, -40.3) * mm});
            skArc(sketch, "E79.18", {"start": v(-60, -40.3) * mm, "mid": v(-58.99, -44.68) * mm, "end": v(-56.15, -48.18) * mm});
            skArc(sketch, "E79.19", {"start": v(56.15, -48.18) * mm, "mid": v(58.99, -44.68) * mm, "end": v(60, -40.3) * mm});
            skLineSegment(sketch, "E80", {"start": v(-33.71, 90) * mm, "end": v(-15, 108.71) * mm});
            skLineSegment(sketch, "E81", {"start": v(-15, 108.71) * mm, "end": v(-15, 120) * mm});
            skArc(sketch, "E82", {"start": v(15, 120) * mm, "mid": v(0, 135) * mm, "end": v(-15, 120) * mm});
            skLineSegment(sketch, "E83", {"start": v(15, 120) * mm, "end": v(15, 108.71) * mm});
            skLineSegment(sketch, "E84", {"start": v(15, 108.71) * mm, "end": v(33.71, 90) * mm});
            skCircle(sketch, "E85", {"center": v(0, 120) * mm, "radius": 6 * mm});
            skLineSegment(sketch, "E86", {"start": v(0, 120) * mm, "end": v(0, 90) * mm, "construction": true});
            skLineSegment(sketch, "E87", {"start": v(-80, 0) * mm, "end": v(80, 0) * mm, "construction": true});
            skLineSegment(sketch, "E88.MirrorCS", {"start": v(-33.71, -90) * mm, "end": v(-15, -108.71) * mm});
            skLineSegment(sketch, "E89.MirrorCS", {"start": v(-15, -108.71) * mm, "end": v(-15, -120) * mm});
            skArc(sketch, "E90.MirrorCS", {"start": v(15, -120) * mm, "mid": v(0, -135) * mm, "end": v(-15, -120) * mm});
            skCircle(sketch, "E91.MirrorC", {"center": v(0, -120) * mm, "radius": 6 * mm});
            skLineSegment(sketch, "E92.MirrorCS", {"start": v(15, -120) * mm, "end": v(15, -108.71) * mm});
            skLineSegment(sketch, "E93.MirrorCS", {"start": v(15, -108.71) * mm, "end": v(33.71, -90) * mm});
            skLineSegment(sketch, "E94.MirrorCS", {"start": v(0, -120) * mm, "end": v(0, -90) * mm, "construction": true});
            skSolve(sketch);
        }
        {
            var Q0;
            Q0 = qSketchRegion(id + "F16", true);
            var Q1;
            Q1=makeQuery(id+"F2.opExtrude","CAP_FACE",FACE,{"disambiguationData":[OSD([sQuery(id+"F0.wireOp",EDGE,"E12"),sQuery(id+"F0.wireOp",EDGE,"E13"),sQuery(id+"F0.wireOp",EDGE,"E14"),sQuery(id+"F0.wireOp",EDGE,"E15"),sQuery(id+"F0.wireOp",EDGE,"E17.filletArc"),sQuery(id+"F0.wireOp",EDGE,"E18.filletArc"),sQuery(id+"F0.wireOp",EDGE,"E19.filletArc"),sQuery(id+"F0.wireOp",EDGE,"E20.filletArc"),sQuery(id+"F0.wireOp",EDGE,"E25.0"),sQuery(id+"F0.wireOp",EDGE,"E25.1"),sQuery(id+"F0.wireOp",EDGE,"E25.2"),sQuery(id+"F0.wireOp",EDGE,"E25.3"),sQuery(id+"F0.wireOp",EDGE,"E25.4"),sQuery(id+"F0.wireOp",EDGE,"E25.5"),sQuery(id+"F0.wireOp",EDGE,"E25.6"),sQuery(id+"F0.wireOp",EDGE,"E25.7")])],"isStart":false});
            extrude(context, id + "F17", {"entities" : qUnion([Q0]), "endBound" : BoundingType.UP_TO_SURFACE, "endBoundEntityFace" : qUnion([Q1]), "depth" : 25 * mm});
        }
    });
